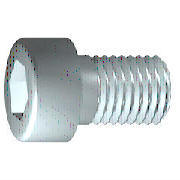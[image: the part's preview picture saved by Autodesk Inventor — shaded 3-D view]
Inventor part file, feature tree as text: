
AUTODESK INVENTOR PART (.ipt)
format: ipt  version: 2017 (Build 210142000, 142)  size: 184,832 bytes
history: native  units: mm (DEFAULTED — no unit token found)
features: sketch x2, extrude x1, plane x1, fillet x1
ambient origin geometry x7: Origin, YZ Plane, XY Plane, X Axis, Y Axis, Z Axis, Center Point
bodies: Solid1 (feature_tree), Body (feature_tree)
feature tree (5):
  extrude  "Slot"  Depth=3.0mm
  plane  "Work Plane1"
  fillet  "Fillet2"  Radius=3.0mm
  sketch  "Sketch1"  dims[d1=18.0mm d2=0.306825mm d3=3.0mm]
  sketch  "Sketch2"  dims[d4=1.5mm d5=60.0deg d6=3.0mm d7=3.0mm d8=2.886751mm d9=5.5mm d10=90.0deg d11=10.0mm d12=0.0mm d13=18.0mm d14=0.0mm d15=0.306725mm d16=0.306725mm d17=0.3mm d19=0.0mm d26=25.0mm d27=45.0deg d28=0.0mm d29=0.0mm d30=0.1mm]
